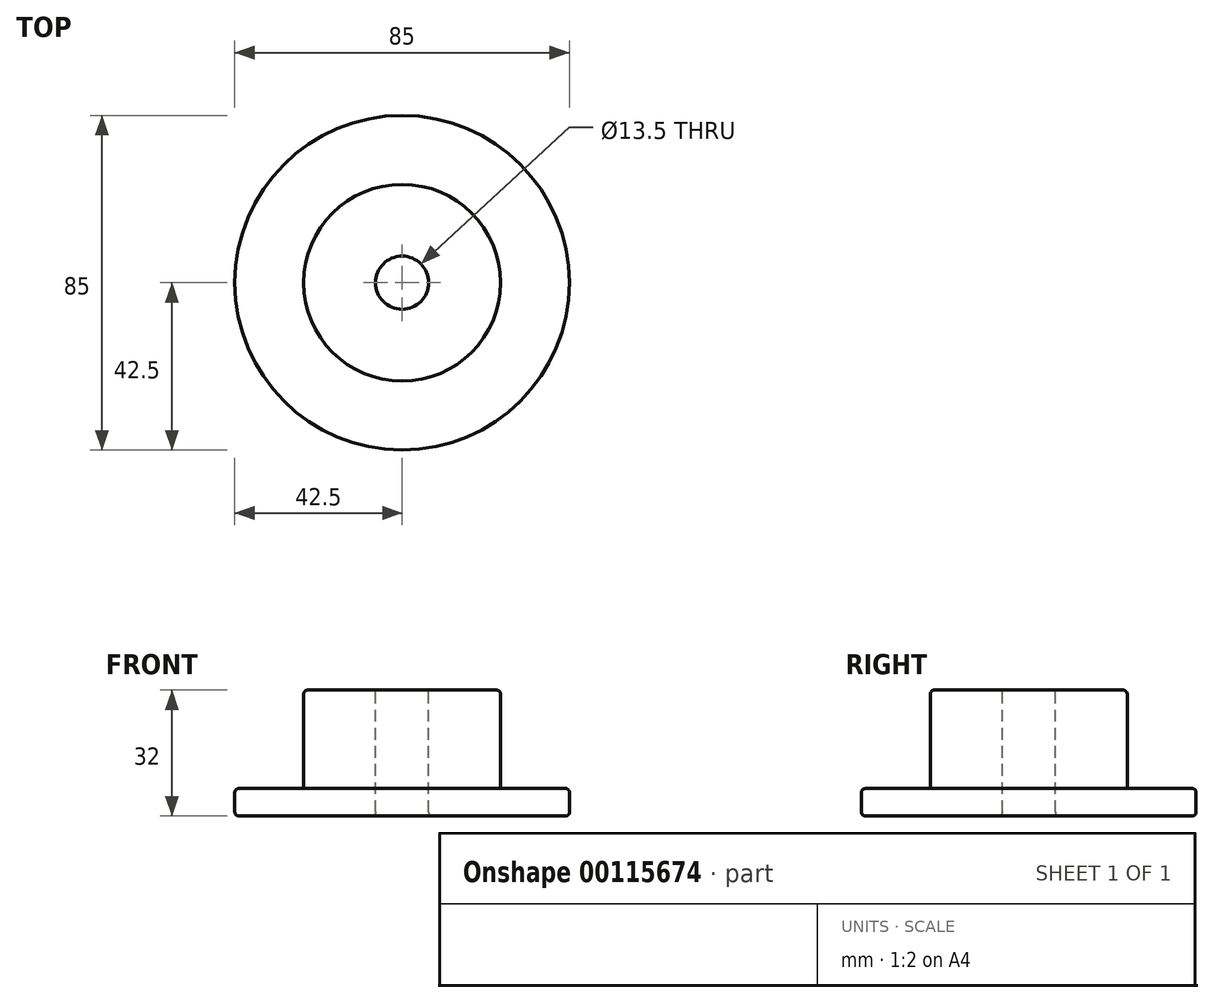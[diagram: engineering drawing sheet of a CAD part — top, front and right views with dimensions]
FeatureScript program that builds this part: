
annotation { "Feature Type Name" : "Feature", "Feature Type Description" : "" }
export const myFeature = defineFeature(function(context is Context, id is Id, definition is map)
    precondition{}
    {
        {
            var Q0;
            Q0=qCreatedBy(makeId("Top.planeOp"),FACE);
            var sketch = newSketch(context, id + "F0", { "sketchPlane" : qUnion([Q0])});
            skCircle(sketch, "E0", {"center": v(0, 0) * mm, "radius": 42.5 * mm});
            skSolve(sketch);
        }
        {
            var Q0;
            Q0 = qSketchRegion(id + "F0", true);
            extrude(context, id + "F1", {"entities" : qUnion([Q0]), "depth" : 7 * mm});
        }
        {
            var Q0;
            Q0=makeQuery(id+"F1.opExtrude","CAP_FACE",FACE,{"disambiguationData":[OSD([sQuery(id+"F0.wireOp",EDGE,"E0")])],"isStart":false});
            var sketch = newSketch(context, id + "F2", { "sketchPlane" : qUnion([Q0])});
            skCircle(sketch, "E1", {"center": v(0, 0) * mm, "radius": 25 * mm});
            skSolve(sketch);
        }
        {
            var Q0;
            Q0 = qSketchRegion(id + "F2", true);
            extrude(context, id + "F3", {"entities" : qUnion([Q0]), "operationType" : NewBodyOperationType.ADD, "depth" : 25 * mm});
        }
        {
            var Q0;
            Q0=makeQuery(id+"F3.opExtrude","CAP_FACE",FACE,{"disambiguationData":[OSD([sQuery(id+"F2.wireOp",EDGE,"E1")])],"isStart":false});
            var sketch = newSketch(context, id + "F4", { "sketchPlane" : qUnion([Q0])});
            skCircle(sketch, "E2", {"center": v(0, 0) * mm, "radius": 6.75 * mm});
            skSolve(sketch);
        }
        {
            var Q0;
            Q0 = qSketchRegion(id + "F4", true);
            extrude(context, id + "F5", {"entities" : qUnion([Q0]), "operationType" : NewBodyOperationType.REMOVE, "endBound" : BoundingType.THROUGH_ALL, "oppositeDirection" : true, "depth" : 25 * mm});
        }
        {
            var Q0;
            Q0=makeQuery(id+"F5.boolean.opBoolean","COPY",EDGE,{"derivedFrom":makeQuery(id+"F5.opExtrude","CAP_EDGE",EDGE,{"disambiguationData":[OSD([sQuery(id+"F4.wireOp",EDGE,"E2")])],"isStart":true})});
            var Q1;
            Q1=makeQuery(id+"F5.boolean.opBoolean","INTERSECT",EDGE,{"derivedFrom":[makeQuery(id+"F1.opExtrude","CAP_FACE",FACE,{"disambiguationData":[OSD([sQuery(id+"F0.wireOp",EDGE,"E0")])],"isStart":true}),makeQuery(id+"F5.opExtrude","SWEPT_FACE",FACE,{"disambiguationData":[OSD([sQuery(id+"F4.wireOp",EDGE,"E2")])]})]});
            var Q2;
            Q2=makeQuery(id+"F1.opExtrude","CAP_EDGE",EDGE,{"disambiguationData":[OSD([sQuery(id+"F0.wireOp",EDGE,"E0")])],"isStart":true});
            var Q3;
            Q3=makeQuery(id+"F1.opExtrude","CAP_EDGE",EDGE,{"disambiguationData":[OSD([sQuery(id+"F0.wireOp",EDGE,"E0")])],"isStart":false});
            var Q4;
            Q4=makeQuery(id+"F3.opExtrude","CAP_EDGE",EDGE,{"disambiguationData":[OSD([sQuery(id+"F2.wireOp",EDGE,"E1")])],"isStart":false});
            fillet(context, id + "F6", {"entities" : qUnion([Q0, Q1, Q2, Q3, Q4]), "radius" : 1 * mm, "tangentPropagation" : true, "allowEdgeOverflow" : false});
        }
    });
